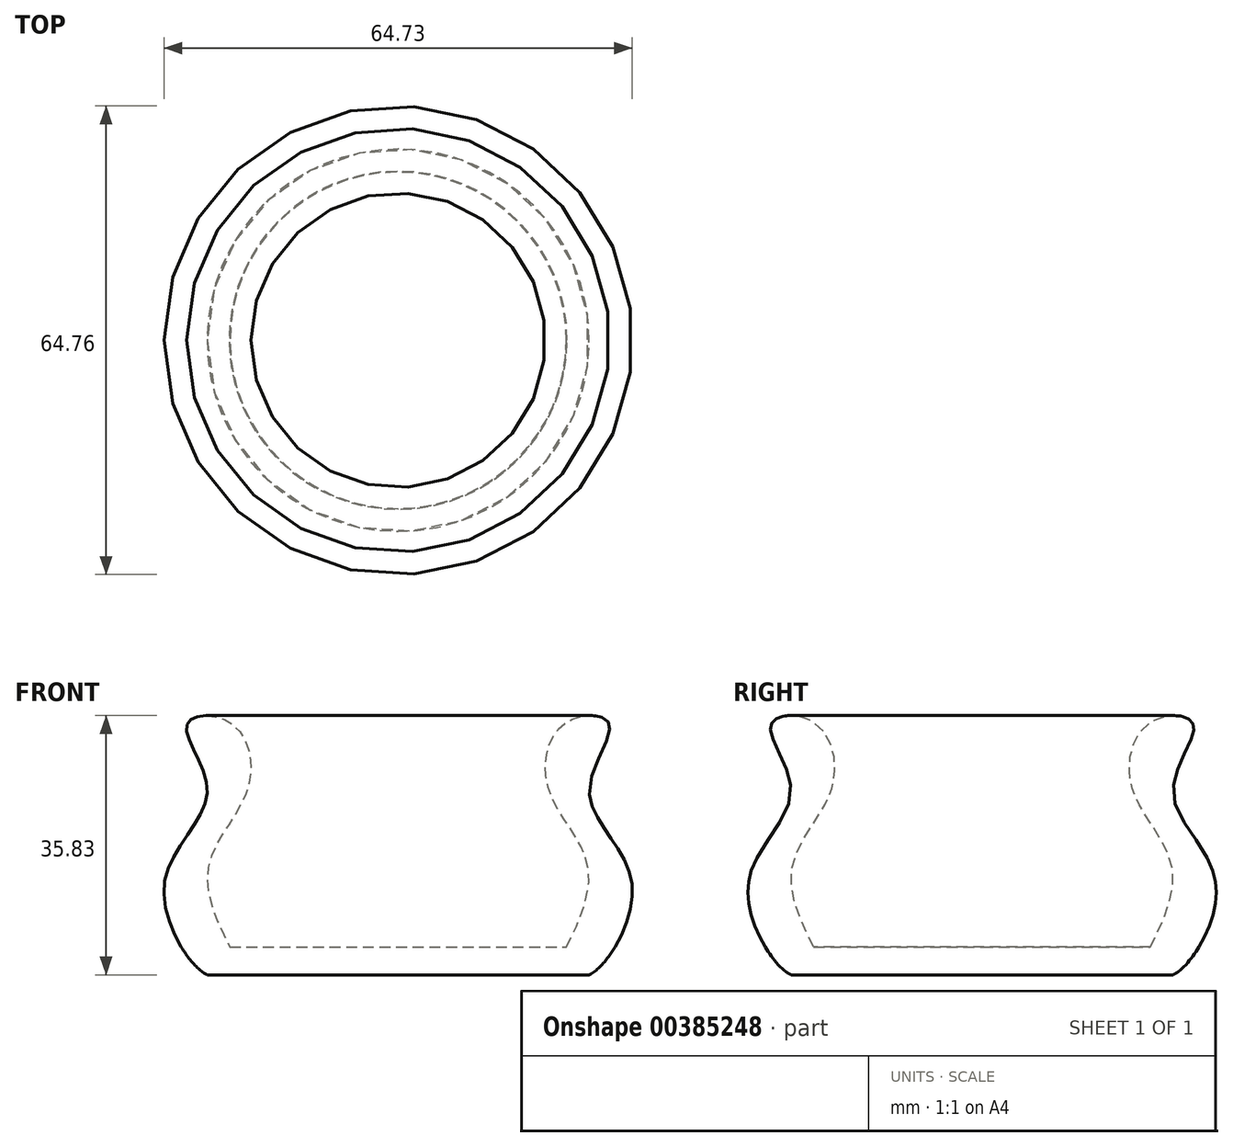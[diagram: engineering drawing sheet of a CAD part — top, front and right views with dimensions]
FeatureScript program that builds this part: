
annotation { "Feature Type Name" : "Feature", "Feature Type Description" : "" }
export const myFeature = defineFeature(function(context is Context, id is Id, definition is map)
    precondition{}
    {
        {
            var Q0;
            Q0=qCreatedBy(makeId("Front.planeOp"),FACE);
            var sketch = newSketch(context, id + "F0", { "sketchPlane" : qUnion([Q0])});
            skLineSegment(sketch, "E0", {"start": v(0, -19.5) * mm, "end": v(-26.4, -19.5) * mm});
            skFitSpline(sketch, "E1", {"points": [v(-26.4, -19.5) * mm, v(-32.32, -6.9) * mm, v(-26.4, 5.91) * mm, v(-29.17, 15.17) * mm, v(-23.25, 15.37) * mm, v(-20.89, 5.91) * mm, v(-26.4, -6.7) * mm, v(-21.68, -19.5) * mm, v(-23.25, -19.5) * mm, v(-26.4, -19.5) * mm]});
            skLineSegment(sketch, "E2", {"start": v(-29.98, -15.66) * mm, "end": v(-23.28, -15.66) * mm});
            skLineSegment(sketch, "E3", {"start": v(-23.28, -15.66) * mm, "end": v(0, -15.66) * mm});
            skLineSegment(sketch, "E4", {"start": v(0, -15.66) * mm, "end": v(0, -19.5) * mm});
            skSolve(sketch);
        }
        {
            var Q0;
            Q0=qCreatedBy(makeId("Front.planeOp"),FACE);
            var sketch = newSketch(context, id + "F1", { "sketchPlane" : qUnion([Q0])});
            skLineSegment(sketch, "E5", {"start": v(0, -19.5) * mm, "end": v(0, 27.2) * mm, "construction": true});
            skSolve(sketch);
        }
        {
            var Q0;
            {var subQ0=sQuery(id+"F0.wireOp",EDGE,"E2");Q0=makeQuery(id+"F0.imprint","IMPRINT",FACE,{"disambiguationData":[TD([[makeQuery(id+"F0.imprint","IMPRINT",EDGE,{"derivedFrom":subQ0}),1.0]])]});}
            var Q1;
            {var subQ3=sQuery(id+"F0.wireOp",EDGE,"E2");Q1=makeQuery(id+"F0.imprint","IMPRINT",FACE,{"disambiguationData":[TD([[makeQuery(id+"F0.imprint","IMPRINT",EDGE,{"derivedFrom":subQ3}),-1.0]])]});}
            var Q2;
            {var subQ4=sQuery(id+"F0.wireOp",EDGE,"E3");Q2=makeQuery(id+"F0.imprint","IMPRINT",FACE,{"disambiguationData":[TD([[makeQuery(id+"F0.imprint","IMPRINT",EDGE,{"derivedFrom":subQ4}),-1.0]])]});}
            var Q3;
            Q3=sQuery(id+"F1.wireOp",EDGE,"E5");
            revolve(context, id + "F2", {"entities" : qUnion([Q0, Q1, Q2]), "axis" : qUnion([Q3]), "revolveType" : RevolveType.FULL});
        }
    });
